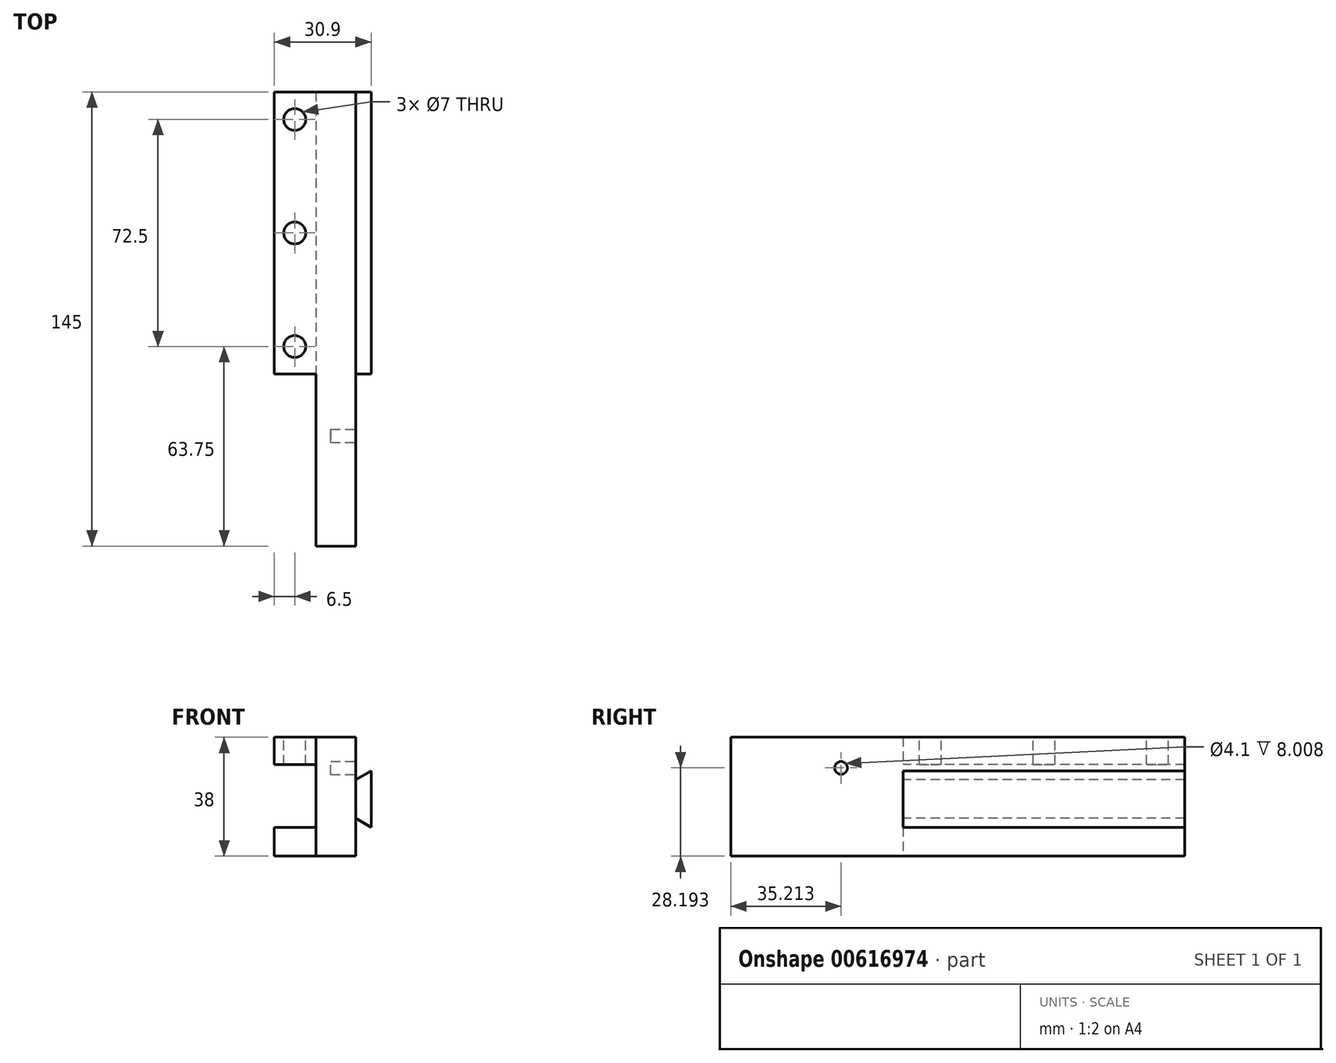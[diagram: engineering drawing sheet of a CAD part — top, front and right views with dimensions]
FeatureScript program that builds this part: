
annotation { "Feature Type Name" : "Feature", "Feature Type Description" : "" }
export const myFeature = defineFeature(function(context is Context, id is Id, definition is map)
    precondition{}
    {
        {
            var Q0;
            Q0=qCreatedBy(makeId("Front.planeOp"),FACE);
            var sketch = newSketch(context, id + "F0", { "sketchPlane" : qUnion([Q0])});
            skLineSegment(sketch, "E0", {"start": v(0, 0) * mm, "end": v(26, 0) * mm});
            skLineSegment(sketch, "E1", {"start": v(26, 0) * mm, "end": v(26, -13.58) * mm});
            skLineSegment(sketch, "E2", {"start": v(26, -13.58) * mm, "end": v(30.9, -10.75) * mm});
            skLineSegment(sketch, "E3", {"start": v(30.9, -10.75) * mm, "end": v(30.9, -28.75) * mm});
            skLineSegment(sketch, "E4", {"start": v(30.9, -28.75) * mm, "end": v(26, -25.92) * mm});
            skLineSegment(sketch, "E5", {"start": v(26, -25.92) * mm, "end": v(26, -38) * mm});
            skLineSegment(sketch, "E6", {"start": v(26, -38) * mm, "end": v(0, -38) * mm});
            skLineSegment(sketch, "E7", {"start": v(0, -38) * mm, "end": v(0, -28.75) * mm});
            skLineSegment(sketch, "E8", {"start": v(0, -28.75) * mm, "end": v(13.25, -28.75) * mm});
            skLineSegment(sketch, "E9", {"start": v(13.25, -28.75) * mm, "end": v(13.25, -8.75) * mm});
            skLineSegment(sketch, "E10", {"start": v(13.25, -8.75) * mm, "end": v(0, -8.75) * mm});
            skLineSegment(sketch, "E11", {"start": v(0, -8.75) * mm, "end": v(0, 0) * mm});
            skLineSegment(sketch, "E12", {"start": v(67.38, -18.75) * mm, "end": v(-31.5, -18.75) * mm, "construction": true});
            skPoint(sketch, "E12.startSnap0", {"position": v(13.25, -18.75) * mm});
            skPoint(sketch, "E12.endSnap0", {"position": v(13.25, -18.75) * mm});
            skSolve(sketch);
        }
        {
            var Q0;
            Q0=makeQuery(id+"F0.imprint","IMPRINT",FACE,{"disambiguationData":[TD([[makeQuery(id+"F0.imprint","IMPRINT",EDGE,{"derivedFrom":sQuery(id+"F0.wireOp",EDGE,"E0")}),-1.0]])]});
            extrude(context, id + "F1", {"entities" : qUnion([Q0]), "oppositeDirection" : true, "depth" : 90 * mm, "offsetDistance" : 25 * mm});
        }
        {
            var Q0;
            Q0=qCreatedBy(makeId("Front.planeOp"),FACE);
            var sketch = newSketch(context, id + "F2", { "sketchPlane" : qUnion([Q0])});
            skLineSegment(sketch, "E13.bottom", {"start": v(26, 0) * mm, "end": v(13.25, 0) * mm});
            skLineSegment(sketch, "E13.top", {"start": v(26, -38) * mm, "end": v(13.25, -38) * mm});
            skLineSegment(sketch, "E13.left", {"start": v(26, 0) * mm, "end": v(26, -38) * mm});
            skLineSegment(sketch, "E13.right", {"start": v(13.25, 0) * mm, "end": v(13.25, -38) * mm});
            skSolve(sketch);
        }
        {
            var Q0;
            Q0=makeQuery(id+"F2.imprint","IMPRINT",FACE,{"disambiguationData":[TD([[makeQuery(id+"F2.imprint","IMPRINT",EDGE,{"derivedFrom":sQuery(id+"F2.wireOp",EDGE,"E13.bottom")}),1.0]])]});
            extrude(context, id + "F3", {"entities" : qUnion([Q0]), "operationType" : NewBodyOperationType.ADD, "depth" : 55 * mm, "offsetDistance" : 25 * mm});
        }
        {
            var Q0;
            Q0=qCreatedBy(makeId("Top.planeOp"),FACE);
            var sketch = newSketch(context, id + "F4", { "sketchPlane" : qUnion([Q0])});
            skCircle(sketch, "E14", {"center": v(6.5, 8.75) * mm, "radius": 3.5 * mm});
            skCircle(sketch, "E15.0.1.0", {"center": v(6.5, 45) * mm, "radius": 3.5 * mm});
            skCircle(sketch, "E15.0.2.0", {"center": v(6.5, 81.25) * mm, "radius": 3.5 * mm});
            skLineSegment(sketch, "E15.direction1", {"start": v(6.5, 8.75) * mm, "end": v(31.5, 8.75) * mm, "construction": true});
            skLineSegment(sketch, "E15.direction2", {"start": v(6.5, 8.75) * mm, "end": v(6.5, 45) * mm, "construction": true});
            skSolve(sketch);
        }
        {
            var Q0;
            Q0=sQuery(id+"F4.wireOp",VERTEX,"E14.center");
            var Q1;
            Q1=makeQuery(id+"F1.opExtrude","SWEPT_BODY",BODY,{"disambiguationData":[OSD([sQuery(id+"F0.wireOp",EDGE,"E0"),sQuery(id+"F0.wireOp",EDGE,"E1"),sQuery(id+"F0.wireOp",EDGE,"E2"),sQuery(id+"F0.wireOp",EDGE,"E3"),sQuery(id+"F0.wireOp",EDGE,"E4"),sQuery(id+"F0.wireOp",EDGE,"E5"),sQuery(id+"F0.wireOp",EDGE,"E6"),sQuery(id+"F0.wireOp",EDGE,"E7"),sQuery(id+"F0.wireOp",EDGE,"E8"),sQuery(id+"F0.wireOp",EDGE,"E9"),sQuery(id+"F0.wireOp",EDGE,"E10"),sQuery(id+"F0.wireOp",EDGE,"E11")])]});
            hole(context, id + "F5", {"style" : HoleStyle.SIMPLE, "endStyle" : HoleEndStyle.BLIND, "standardTappedOrClearance" : lookupTablePath({ "standard" : "ISO", "engagement" : "75%", "pitch" : "1 mm", "size" : "M8", "type" : "Tapped" }), "standardBlindInLast" : lookupTablePath({ "standard" : "ISO", "engagement" : "75%", "pitch" : "1 mm", "size" : "M8", "type" : "Tapped" }), "holeDiameter" : 7 * mm, "majorDiameter" : 8 * mm, "showTappedDepth" : true, "holeDepth" : 13 * mm, "tappedDepth" : 10 * mm, "tapClearance" : 3, "startFromSketch" : true, "locations" : qUnion([Q0]), "scope" : qUnion([Q1])});
        }
        {
            var Q0;
            Q0=sQuery(id+"F4.wireOp",VERTEX,"E15.0.1.0.center");
            var Q1;
            Q1=makeQuery(id+"F1.opExtrude","SWEPT_BODY",BODY,{"disambiguationData":[OSD([sQuery(id+"F0.wireOp",EDGE,"E0"),sQuery(id+"F0.wireOp",EDGE,"E1"),sQuery(id+"F0.wireOp",EDGE,"E2"),sQuery(id+"F0.wireOp",EDGE,"E3"),sQuery(id+"F0.wireOp",EDGE,"E4"),sQuery(id+"F0.wireOp",EDGE,"E5"),sQuery(id+"F0.wireOp",EDGE,"E6"),sQuery(id+"F0.wireOp",EDGE,"E7"),sQuery(id+"F0.wireOp",EDGE,"E8"),sQuery(id+"F0.wireOp",EDGE,"E9"),sQuery(id+"F0.wireOp",EDGE,"E10"),sQuery(id+"F0.wireOp",EDGE,"E11")])]});
            hole(context, id + "F6", {"style" : HoleStyle.SIMPLE, "endStyle" : HoleEndStyle.BLIND, "standardTappedOrClearance" : lookupTablePath({ "standard" : "ISO", "engagement" : "75%", "pitch" : "1 mm", "size" : "M8", "type" : "Tapped" }), "standardBlindInLast" : lookupTablePath({ "standard" : "ISO", "engagement" : "75%", "pitch" : "1 mm", "size" : "M8", "type" : "Tapped" }), "holeDiameter" : 7 * mm, "majorDiameter" : 8 * mm, "showTappedDepth" : true, "holeDepth" : 9.25 * mm, "tappedDepth" : 6.25 * mm, "tapClearance" : 3, "startFromSketch" : true, "locations" : qUnion([Q0]), "scope" : qUnion([Q1])});
        }
        {
            var Q0;
            Q0=sQuery(id+"F4.wireOp",VERTEX,"E15.0.2.0.center");
            var Q1;
            Q1=makeQuery(id+"F1.opExtrude","SWEPT_BODY",BODY,{"disambiguationData":[OSD([sQuery(id+"F0.wireOp",EDGE,"E0"),sQuery(id+"F0.wireOp",EDGE,"E1"),sQuery(id+"F0.wireOp",EDGE,"E2"),sQuery(id+"F0.wireOp",EDGE,"E3"),sQuery(id+"F0.wireOp",EDGE,"E4"),sQuery(id+"F0.wireOp",EDGE,"E5"),sQuery(id+"F0.wireOp",EDGE,"E6"),sQuery(id+"F0.wireOp",EDGE,"E7"),sQuery(id+"F0.wireOp",EDGE,"E8"),sQuery(id+"F0.wireOp",EDGE,"E9"),sQuery(id+"F0.wireOp",EDGE,"E10"),sQuery(id+"F0.wireOp",EDGE,"E11")])]});
            hole(context, id + "F7", {"style" : HoleStyle.SIMPLE, "endStyle" : HoleEndStyle.BLIND, "standardTappedOrClearance" : lookupTablePath({ "standard" : "ISO", "engagement" : "75%", "pitch" : "1 mm", "size" : "M8", "type" : "Tapped" }), "standardBlindInLast" : lookupTablePath({ "standard" : "ISO", "engagement" : "75%", "pitch" : "1 mm", "size" : "M8", "type" : "Tapped" }), "holeDiameter" : 7 * mm, "majorDiameter" : 8 * mm, "showTappedDepth" : true, "holeDepth" : 13 * mm, "tappedDepth" : 10 * mm, "tapClearance" : 3, "startFromSketch" : true, "locations" : qUnion([Q0]), "scope" : qUnion([Q1])});
        }
        {
            var Q0;
            Q0=qCreatedBy(makeId("Right.planeOp"),FACE);
            cPlane(context, id + "F8", {"entities" : qUnion([Q0]), "cplaneType" : CPlaneType.OFFSET, "offset" : 26 * mm, "width" : 150 * mm, "height" : 150 * mm});
        }
        {
            var Q0;
            Q0=qCreatedBy(id+"F8.planeOp",FACE);
            var sketch = newSketch(context, id + "F9", { "sketchPlane" : qUnion([Q0])});
            skCircle(sketch, "E16", {"center": v(-19.79, -9.8) * mm, "radius": 2.05 * mm});
            skLineSegment(sketch, "E17", {"start": v(-27.5, 19.45) * mm, "end": v(-27.5, -51.51) * mm, "construction": true});
            skLineSegment(sketch, "E18", {"start": v(-64.33, -19) * mm, "end": v(99.03, -19) * mm, "construction": true});
            skPoint(sketch, "E19", {"position": v(-27.5, -19) * mm});
            skLineSegment(sketch, "E20", {"start": v(-27.5, -19) * mm, "end": v(-19.79, -9.8) * mm, "construction": true});
            skSolve(sketch);
        }
        {
            var Q0;
            Q0=makeQuery(id+"F9.imprint","IMPRINT",FACE,{"disambiguationData":[TD([[makeQuery(id+"F9.imprint","IMPRINT",EDGE,{"derivedFrom":sQuery(id+"F9.wireOp",EDGE,"E16")}),1.0]])]});
            extrude(context, id + "F10", {"entities" : qUnion([Q0]), "operationType" : NewBodyOperationType.REMOVE, "oppositeDirection" : true, "depth" : 8 * mm, "offsetDistance" : 25 * mm});
        }
    });
